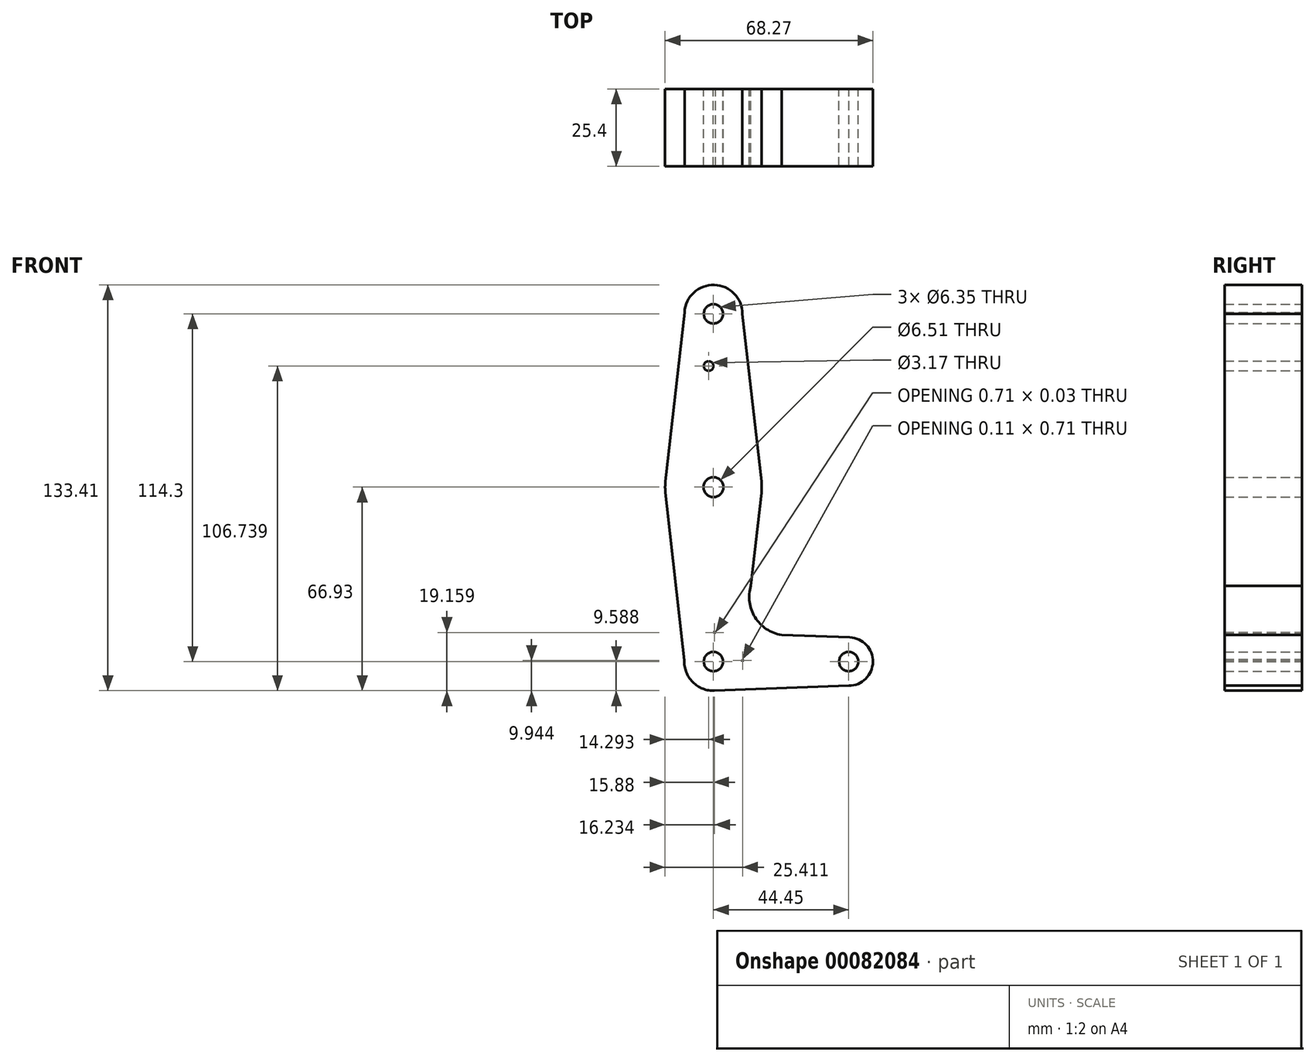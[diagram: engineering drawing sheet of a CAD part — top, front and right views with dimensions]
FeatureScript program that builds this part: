
annotation { "Feature Type Name" : "Feature", "Feature Type Description" : "" }
export const myFeature = defineFeature(function(context is Context, id is Id, definition is map)
    precondition{}
    {
        {
            var Q0;
            Q0=qCreatedBy(makeId("Front.planeOp"),FACE);
            var sketch = newSketch(context, id + "F0", { "sketchPlane" : qUnion([Q0])});
            skCircle(sketch, "E0", {"center": v(0, 56.96) * mm, "radius": 9.53 * mm});
            skCircle(sketch, "E1", {"center": v(0, -57.34) * mm, "radius": 9.58 * mm});
            skCircle(sketch, "E2", {"center": v(44.45, -57.34) * mm, "radius": 7.94 * mm});
            skCircle(sketch, "E3", {"center": v(0, 0) * mm, "radius": 15.88 * mm});
            skLineSegment(sketch, "E4", {"start": v(9.52, 56.92) * mm, "end": v(15.98, 0) * mm});
            skLineSegment(sketch, "E5", {"start": v(-9.51, 57.48) * mm, "end": v(-15.98, 0) * mm});
            skLineSegment(sketch, "E6", {"start": v(15.98, 0) * mm, "end": v(12.3, -32.44) * mm});
            skLineSegment(sketch, "E7", {"start": v(-15.98, 0) * mm, "end": v(-9.57, -56.9) * mm});
            skLineSegment(sketch, "E8", {"start": v(0, 0) * mm, "end": v(0, -0.2) * mm, "construction": true});
            skLineSegment(sketch, "E9", {"start": v(0, -47.76) * mm, "end": v(0.7, -47.78) * mm});
            skLineSegment(sketch, "E10", {"start": v(44.45, -65.28) * mm, "end": v(0, -66.93) * mm});
            skCircle(sketch, "E11", {"center": v(0, 56.96) * mm, "radius": 3.18 * mm});
            skArc(sketch, "E12", {"start": v(12.3, -32.44) * mm, "mid": v(13.67, -42.8) * mm, "end": v(22.37, -48.58) * mm});
            skLineSegment(sketch, "E13.trimOffspring", {"start": v(9.56, -56.63) * mm, "end": v(9.48, -57.34) * mm});
            skLineSegment(sketch, "E14.trimOffspring", {"start": v(22.37, -48.58) * mm, "end": v(44.74, -49.41) * mm});
            skCircle(sketch, "E15", {"center": v(-1.59, 39.8) * mm, "radius": 1.59 * mm});
            skCircle(sketch, "E16", {"center": v(0, 0) * mm, "radius": 3.25 * mm});
            skCircle(sketch, "E17", {"center": v(0, -57.34) * mm, "radius": 3.18 * mm});
            skCircle(sketch, "E18", {"center": v(44.45, -57.34) * mm, "radius": 3.18 * mm});
            skLineSegment(sketch, "E19.trimOffspring", {"start": v(0, 0) * mm, "end": v(0, -0.2) * mm});
            skLineSegment(sketch, "E20.trimOffspring", {"start": v(9.48, -57.34) * mm, "end": v(9.58, -57.34) * mm});
            skLineSegment(sketch, "E21.trimOffspring", {"start": v(0, -47.76) * mm, "end": v(0, -57.34) * mm, "construction": true});
            skSolve(sketch);
        }
        {
            var Q0;
            Q0=makeQuery(id+"F0.imprint","IMPRINT",FACE,{"disambiguationData":[TD([[makeQuery(id+"F0.imprint","IMPRINT",EDGE,{"derivedFrom":sQuery(id+"F0.wireOp",EDGE,"E15")}),-1.0]])]});
            var Q1;
            Q1=makeQuery(id+"F0.imprint","IMPRINT",FACE,{"disambiguationData":[TD([[makeQuery(id+"F0.imprint","IMPRINT",EDGE,{"derivedFrom":sQuery(id+"F0.wireOp",EDGE,"E16")}),-1.0]])]});
            var Q2;
            {var subQ0=sQuery(id+"F0.wireOp",EDGE,"E12");Q2=makeQuery(id+"F0.imprint","IMPRINT",FACE,{"disambiguationData":[TD([[makeQuery(id+"F0.imprint","IMPRINT",EDGE,{"derivedFrom":subQ0}),-1.0]])]});}
            var Q3;
            Q3=makeQuery(id+"F0.imprint","IMPRINT",FACE,{"disambiguationData":[TD([[makeQuery(id+"F0.imprint","IMPRINT",EDGE,{"derivedFrom":sQuery(id+"F0.wireOp",EDGE,"E18")}),-1.0]])]});
            var Q4;
            {var subQ4=sQuery(id+"F0.wireOp",EDGE,"E9");Q4=makeQuery(id+"F0.imprint","IMPRINT",FACE,{"disambiguationData":[TD([[makeQuery(id+"F0.imprint","IMPRINT",EDGE,{"derivedFrom":subQ4}),-1.0]])]});}
            var Q5;
            Q5=makeQuery(id+"F0.imprint","IMPRINT",FACE,{"disambiguationData":[TD([[makeQuery(id+"F0.imprint","IMPRINT",EDGE,{"derivedFrom":sQuery(id+"F0.wireOp",EDGE,"E11")}),-1.0]])]});
            extrude(context, id + "F1", {"entities" : qUnion([Q0, Q1, Q2, Q3, Q4, Q5]), "depth" : 25.4 * mm});
        }
    });
